# Revit family: Sliding_Glass-Pocket-PGT-Aluminum_Preferred-SGD770-Xd
name_source: partatom
category: Doors
revit_build: Autodesk Revit 2015 (Build: 20160512_1515(x64)
units: mm (PartAtom-declared; Revit-internal decimal feet)

## types (1)
- Refer to Type Catalog
    Analytic Construction = <None>
    Assembly Code = B2030110
    Box Riser = No
    Color Glass = Glass - PGT - Clear
    Custom Design Note = The types included show default grid/size configurations.  Please reference the 'Product Style Guide' to see all standard configurations and restrictions before creating custom designs.  Please contact PGT Industries with any questions regarding custom designs.
    Description = Aluminum Preferred Siding Glass Door
    Door Panel Height = 120"
    Door Panel Width = 60"
    Finish = Metal - PGT - Paint - White
    Finished Opening = 58 1/8"
    Flush Riser = Yes
    Function = Exterior
    Glass Thickness = 1"
    Glass Width = 53 1/8"
    Grid = Yes
    Grid Layout Note = To edit the grid layout ensure the 'Grid' parameter is turned on and then select an option from the 'Grid Type' drop down.  Please refer to the 'Product Style Guide' for standard configurations and restrictions.
    Grid Type = Face_Based_Mullion_ Glass : BP9
    Hardware Height = 36"
    Hardware Material = Steel AISI 4620
    Height = 121 7/8"
    High Riser = No
    Low Riser = No
    Manufacturer = PGT Industries
    Maximum Panel Size = 4' x 10' OR 5' x 8'
    Medium Riser = No
    Minimum Panel Size = 21 1/2” x 32 5/8”
    Model = SGD770 1P1T X
    Narrow Riser = Yes
    Plan Detail Offset = 19 3/8"
    Pocket Width = 65 1/8"
    Product Page URL = http://www.pgtindustries.com
    Product Style Guide = http://www.pgtindustries.com
    Track Depth = 4 7/8"
    Type Comments = Pocket
    URL = http://www.pgtindustries.com
    Wall Closure = By host
    Width = 123 1/4"

## geometry (parser evidence)
native form markers: Sweep x32
no freeform markers — native parametric forms only
